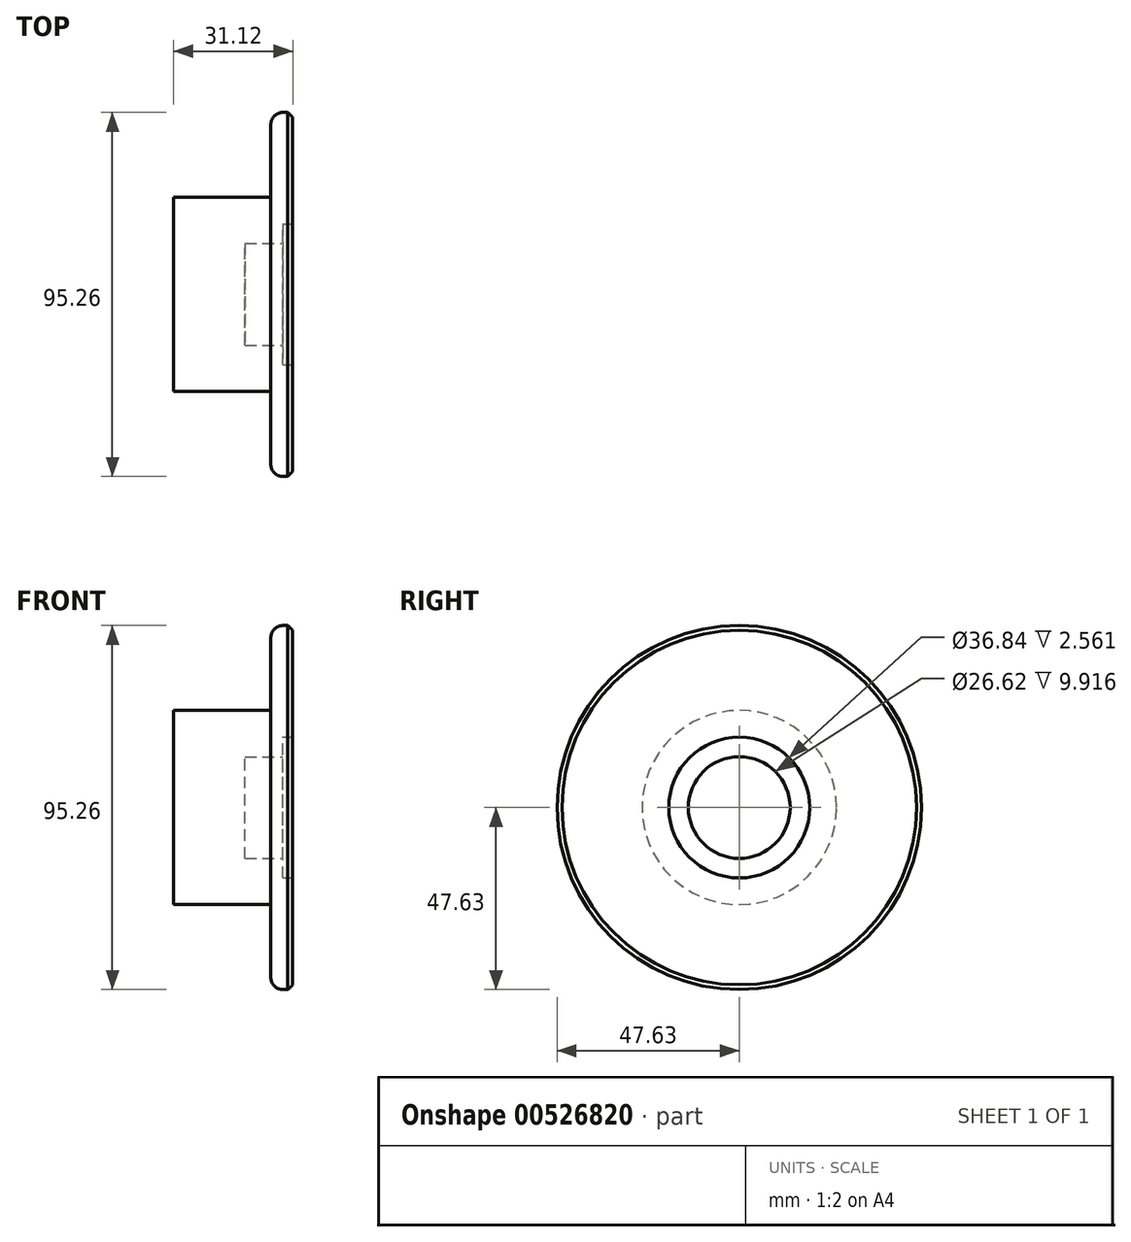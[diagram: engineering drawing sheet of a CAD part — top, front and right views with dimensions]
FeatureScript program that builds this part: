
annotation { "Feature Type Name" : "Feature", "Feature Type Description" : "" }
export const myFeature = defineFeature(function(context is Context, id is Id, definition is map)
    precondition{}
    {
        {
            var Q0;
            Q0=qCreatedBy(makeId("Front.planeOp"),FACE);
            var sketch = newSketch(context, id + "F0", { "sketchPlane" : qUnion([Q0])});
            skLineSegment(sketch, "E0", {"start": v(0, 0) * mm, "end": v(0, -25.4) * mm});
            skLineSegment(sketch, "E1", {"start": v(0, -25.4) * mm, "end": v(25.4, -25.4) * mm});
            skLineSegment(sketch, "E2", {"start": v(25.4, -25.4) * mm, "end": v(25.4, -44.45) * mm});
            skLineSegment(sketch, "E3", {"start": v(18.64, 0) * mm, "end": v(0, 0) * mm});
            skPoint(sketch, "E4.visualSharp", {"position": v(25.4, -47.63) * mm});
            skArc(sketch, "E4.filletArc", {"start": v(25.4, -44.45) * mm, "mid": v(26.32, -46.7) * mm, "end": v(28.57, -47.63) * mm});
            skLineSegment(sketch, "E5", {"start": v(28.57, -47.63) * mm, "end": v(29.84, -47.63) * mm});
            skLineSegment(sketch, "E6", {"start": v(29.84, -47.63) * mm, "end": v(31.12, -46.36) * mm});
            skLineSegment(sketch, "E7", {"start": v(31.12, -46.36) * mm, "end": v(31.12, -18.42) * mm});
            skLineSegment(sketch, "E8", {"start": v(31.12, -18.42) * mm, "end": v(28.56, -18.42) * mm});
            skLineSegment(sketch, "E9", {"start": v(28.56, -18.42) * mm, "end": v(28.56, -13.31) * mm});
            skLineSegment(sketch, "E10", {"start": v(28.56, -13.31) * mm, "end": v(18.64, -13.31) * mm});
            skLineSegment(sketch, "E11", {"start": v(18.64, 0) * mm, "end": v(18.64, -13.31) * mm});
            skSolve(sketch);
        }
        {
            var Q0;
            Q0=makeQuery(id+"F0.imprint","IMPRINT",FACE,{"disambiguationData":[TD([[makeQuery(id+"F0.imprint","IMPRINT",EDGE,{"derivedFrom":sQuery(id+"F0.wireOp",EDGE,"E0")}),1.0]])]});
            var Q1;
            Q1=sQuery(id+"F0.wireOp",EDGE,"E3");
            revolve(context, id + "F1", {"entities" : qUnion([Q0]), "axis" : qUnion([Q1]), "revolveType" : RevolveType.FULL});
        }
    });
